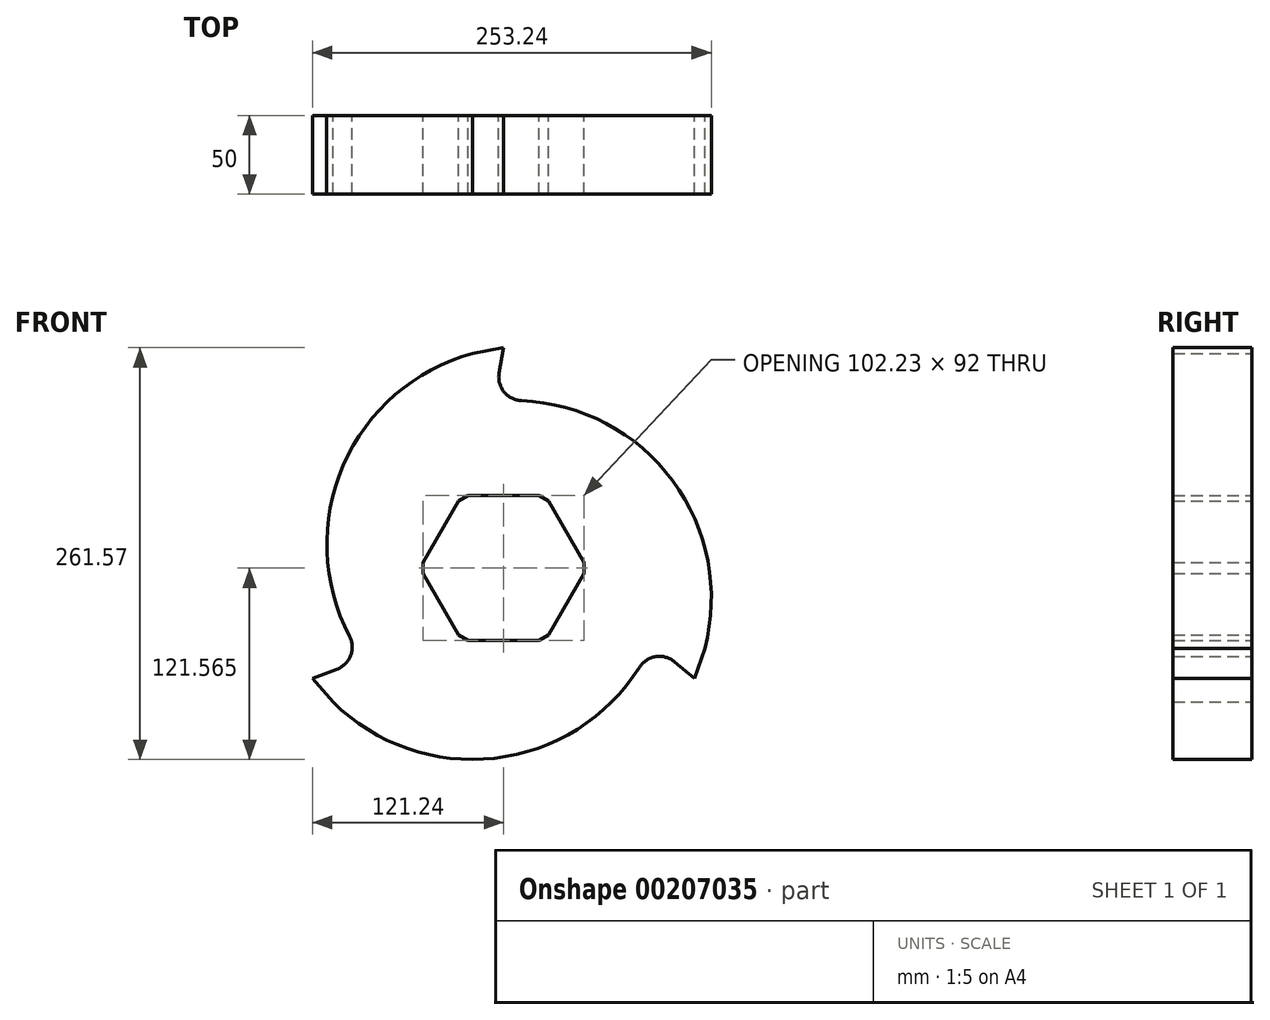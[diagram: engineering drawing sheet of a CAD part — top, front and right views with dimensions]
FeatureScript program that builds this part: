
annotation { "Feature Type Name" : "Feature", "Feature Type Description" : "" }
export const myFeature = defineFeature(function(context is Context, id is Id, definition is map)
    precondition{}
    {
        {
            var Q0;
            Q0=qCreatedBy(makeId("Front.planeOp"),FACE);
            var sketch = newSketch(context, id + "F0", { "sketchPlane" : qUnion([Q0])});
            skLineSegment(sketch, "E0", {"start": v(-716.26, 551.94) * mm, "end": v(-719.03, 535.8) * mm});
            skLineSegment(sketch, "E1", {"start": v(-837.5, 341.94) * mm, "end": v(-822.15, 347.6) * mm});
            skLineSegment(sketch, "E2", {"start": v(-595.02, 341.94) * mm, "end": v(-607.6, 352.4) * mm});
            skArc(sketch, "E3", {"start": v(-735.91, 548.23) * mm, "mid": v(-818.04, 477.18) * mm, "end": v(-814.06, 368.65) * mm});
            skArc(sketch, "E4", {"start": v(-824.47, 326.77) * mm, "mid": v(-721.87, 291.17) * mm, "end": v(-629.88, 348.88) * mm});
            skArc(sketch, "E5", {"start": v(-588.4, 360.8) * mm, "mid": v(-608.87, 467.46) * mm, "end": v(-704.84, 518.28) * mm});
            skLineSegment(sketch, "E6", {"start": v(-716.26, 551.94) * mm, "end": v(-735.91, 548.23) * mm});
            skLineSegment(sketch, "E7", {"start": v(-837.5, 341.94) * mm, "end": v(-824.47, 326.77) * mm});
            skLineSegment(sketch, "E8", {"start": v(-595.02, 341.94) * mm, "end": v(-588.4, 360.8) * mm});
            skArc(sketch, "E9", {"start": v(-822.15, 347.6) * mm, "mid": v(-813.34, 356.3) * mm, "end": v(-814.06, 368.65) * mm});
            skArc(sketch, "E10", {"start": v(-607.6, 352.4) * mm, "mid": v(-619.54, 355.68) * mm, "end": v(-629.88, 348.88) * mm});
            skArc(sketch, "E11", {"start": v(-719.03, 535.8) * mm, "mid": v(-715.9, 523.83) * mm, "end": v(-704.84, 518.28) * mm});
            skLineSegment(sketch, "E12", {"start": v(-744.82, 454.47) * mm, "end": v(-767.38, 415.4) * mm});
            skLineSegment(sketch, "E13", {"start": v(-767.38, 415.4) * mm, "end": v(-767.38, 408.47) * mm});
            skLineSegment(sketch, "E14", {"start": v(-767.38, 408.47) * mm, "end": v(-744.82, 369.4) * mm});
            skLineSegment(sketch, "E15", {"start": v(-744.82, 369.4) * mm, "end": v(-738.82, 365.94) * mm});
            skLineSegment(sketch, "E16", {"start": v(-738.82, 365.94) * mm, "end": v(-693.7, 365.94) * mm});
            skLineSegment(sketch, "E17", {"start": v(-693.7, 365.94) * mm, "end": v(-687.7, 369.4) * mm});
            skLineSegment(sketch, "E18", {"start": v(-687.7, 369.4) * mm, "end": v(-665.14, 408.47) * mm});
            skLineSegment(sketch, "E19", {"start": v(-665.14, 408.47) * mm, "end": v(-665.14, 415.4) * mm});
            skLineSegment(sketch, "E20", {"start": v(-665.14, 415.4) * mm, "end": v(-687.7, 454.47) * mm});
            skLineSegment(sketch, "E21", {"start": v(-687.7, 454.47) * mm, "end": v(-693.7, 457.94) * mm});
            skLineSegment(sketch, "E22", {"start": v(-693.7, 457.94) * mm, "end": v(-738.82, 457.94) * mm});
            skLineSegment(sketch, "E23", {"start": v(-738.82, 457.94) * mm, "end": v(-744.82, 454.47) * mm});
            skSolve(sketch);
        }
        {
            var Q0;
            Q0=makeQuery(id+"F0.imprint","IMPRINT",FACE,{"disambiguationData":[TD([[makeQuery(id+"F0.imprint","IMPRINT",EDGE,{"derivedFrom":sQuery(id+"F0.wireOp",EDGE,"E0")}),-1.0]])]});
            extrude(context, id + "F1", {"entities" : qUnion([Q0]), "depth" : 50 * mm});
        }
    });
